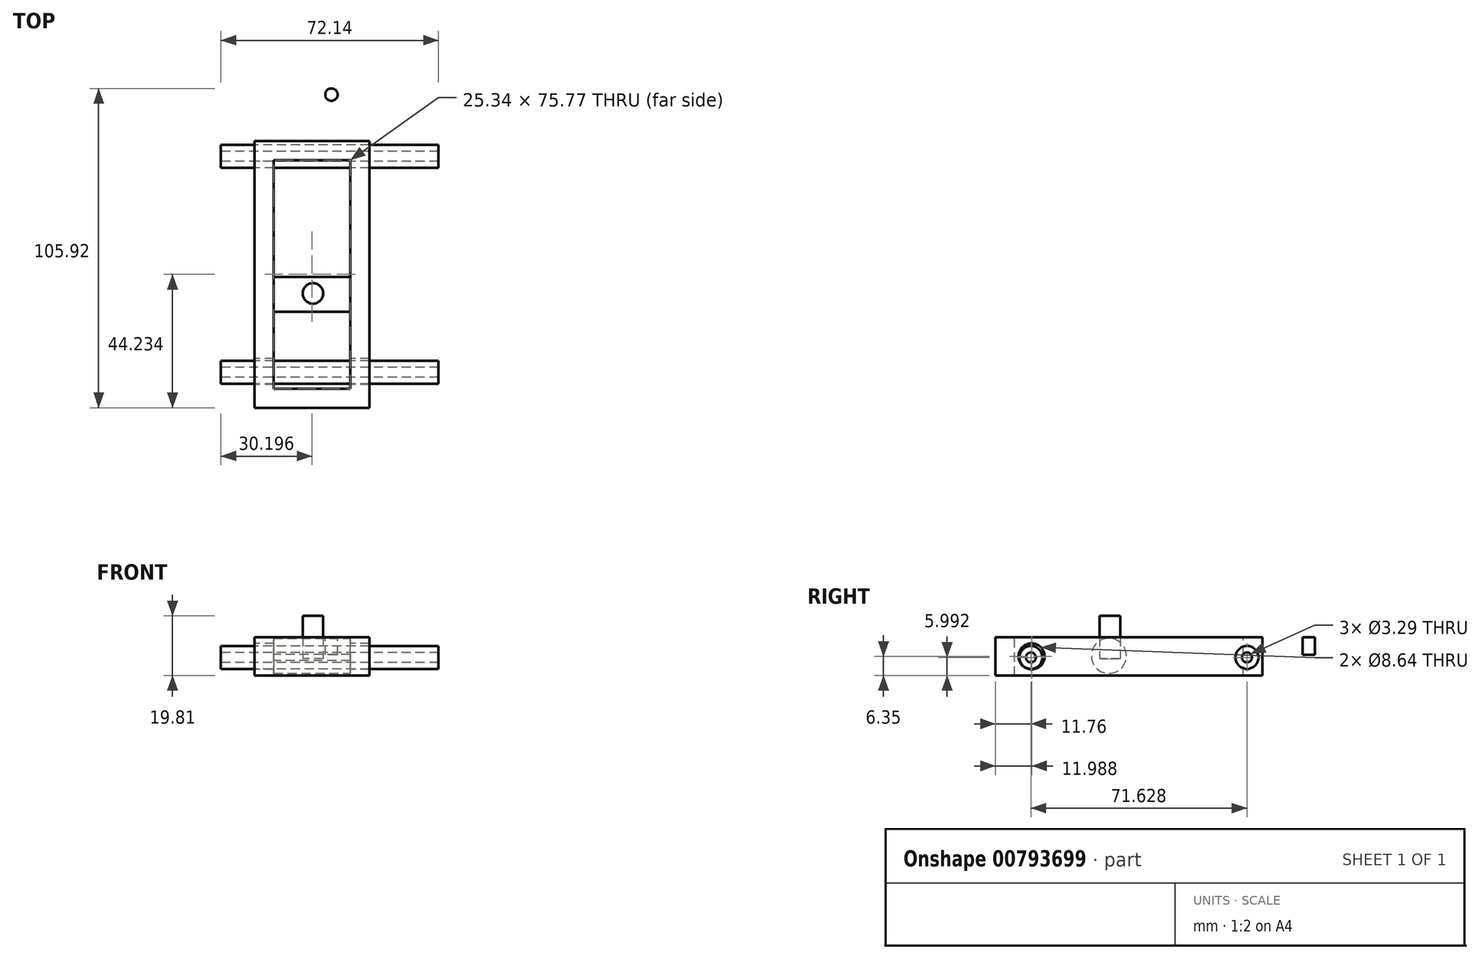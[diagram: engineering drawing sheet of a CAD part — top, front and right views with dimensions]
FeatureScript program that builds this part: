
annotation { "Feature Type Name" : "Feature", "Feature Type Description" : "" }
export const myFeature = defineFeature(function(context is Context, id is Id, definition is map)
    precondition{}
    {
        {
            var Q0;
            Q0=qCreatedBy(makeId("Top.planeOp"),FACE);
            var sketch = newSketch(context, id + "F0", { "sketchPlane" : qUnion([Q0])});
            skLineSegment(sketch, "E0.bottom", {"start": v(-27.68, 27.07) * mm, "end": v(10.35, 27.07) * mm});
            skLineSegment(sketch, "E0.top", {"start": v(-27.68, -61.4) * mm, "end": v(10.35, -61.4) * mm});
            skLineSegment(sketch, "E0.left", {"start": v(-27.68, 27.07) * mm, "end": v(-27.68, -61.4) * mm});
            skLineSegment(sketch, "E0.right", {"start": v(10.35, 27.07) * mm, "end": v(10.35, -61.4) * mm});
            skSolve(sketch);
        }
        {
            var Q0;
            Q0 = qSketchRegion(id + "F0", true);
            extrude(context, id + "F1", {"entities" : qUnion([Q0]), "depth" : 12.7 * mm, "offsetDistance" : 25.4 * mm});
        }
        {
            var Q0;
            Q0=makeQuery(id+"F1.opExtrude","CAP_FACE",FACE,{"disambiguationData":[OSD([sQuery(id+"F0.wireOp",EDGE,"E0.bottom"),sQuery(id+"F0.wireOp",EDGE,"E0.top"),sQuery(id+"F0.wireOp",EDGE,"E0.left"),sQuery(id+"F0.wireOp",EDGE,"E0.right")])],"isStart":false});
            var sketch = newSketch(context, id + "F2", { "sketchPlane" : qUnion([Q0])});
            skLineSegment(sketch, "E1.0", {"start": v(-21.33, 20.72) * mm, "end": v(4, 20.72) * mm});
            skLineSegment(sketch, "E1.1", {"start": v(-21.33, 20.72) * mm, "end": v(-21.33, -55.05) * mm});
            skLineSegment(sketch, "E1.2", {"start": v(-21.33, -55.05) * mm, "end": v(4, -55.05) * mm});
            skLineSegment(sketch, "E1.3", {"start": v(4, 20.72) * mm, "end": v(4, -55.05) * mm});
            skSolve(sketch);
        }
        {
            var Q0;
            Q0=makeQuery(id+"F2.imprint","IMPRINT",FACE,{"disambiguationData":[TD([[makeQuery(id+"F2.imprint","IMPRINT",EDGE,{"derivedFrom":sQuery(id+"F2.wireOp",EDGE,"E1.0")}),-1.0]])]});
            extrude(context, id + "F3", {"entities" : qUnion([Q0]), "operationType" : NewBodyOperationType.REMOVE, "oppositeDirection" : true, "depth" : 25.4 * mm, "offsetDistance" : 25.4 * mm});
        }
        {
            var Q0;
            Q0=makeQuery(id+"F1.opExtrude","SWEPT_FACE",FACE,{"disambiguationData":[OSD([sQuery(id+"F0.wireOp",EDGE,"E0.left")])]});
            var sketch = newSketch(context, id + "F4", { "sketchPlane" : qUnion([Q0])});
            skCircle(sketch, "E2", {"center": v(49.41, 6.35) * mm, "radius": 4.32 * mm});
            skSolve(sketch);
        }
        {
            var Q0;
            Q0 = qSketchRegion(id + "F4", true);
            var Q1;
            Q1=makeQuery(id+"F4.imprint","IMPRINT",FACE,{"disambiguationData":[TD([[makeQuery(id+"F4.imprint","IMPRINT",EDGE,{"derivedFrom":sQuery(id+"F4.wireOp",EDGE,"E2")}),1.0]])]});
            extrude(context, id + "F5", {"entities" : qUnion([Q0, Q1]), "operationType" : NewBodyOperationType.REMOVE, "oppositeDirection" : true, "depth" : 64.52 * mm, "offsetDistance" : 25.4 * mm});
        }
        {
            var Q0;
            Q0=makeQuery(id+"F1.opExtrude","SWEPT_FACE",FACE,{"disambiguationData":[OSD([sQuery(id+"F0.wireOp",EDGE,"E0.left")])]});
            var sketch = newSketch(context, id + "F6", { "sketchPlane" : qUnion([Q0])});
            skCircle(sketch, "E3", {"center": v(-21.99, 6) * mm, "radius": 1.65 * mm});
            skSolve(sketch);
        }
        {
            var Q0;
            Q0 = qSketchRegion(id + "F6", true);
            extrude(context, id + "F7", {"entities" : qUnion([Q0]), "operationType" : NewBodyOperationType.REMOVE, "oppositeDirection" : true, "depth" : 67.3 * mm, "offsetDistance" : 25.4 * mm});
        }
        {
            var Q0;
            Q0=makeQuery(id+"F1.opExtrude","SWEPT_FACE",FACE,{"disambiguationData":[OSD([sQuery(id+"F0.wireOp",EDGE,"E0.left")])]});
            var sketch = newSketch(context, id + "F8", { "sketchPlane" : qUnion([Q0])});
            skCircle(sketch, "E4.0", {"center": v(-21.99, 6) * mm, "radius": 1.65 * mm});
            skCircle(sketch, "E5", {"center": v(-21.99, 6) * mm, "radius": 3.81 * mm});
            skSolve(sketch);
        }
        {
            var Q0;
            Q0=makeQuery(id+"F8.imprint","IMPRINT",FACE,{"disambiguationData":[TD([[makeQuery(id+"F8.imprint","IMPRINT",EDGE,{"derivedFrom":sQuery(id+"F8.wireOp",EDGE,"E5")}),1.0]])]});
            extrude(context, id + "F9", {"entities" : qUnion([Q0]), "oppositeDirection" : true, "depth" : 72.14 * mm, "offsetDistance" : 25.4 * mm});
        }
        {
            var Q0;
            Q0=makeQuery(id+"F9.opExtrude","SWEPT_BODY",BODY,{"disambiguationData":[OSD([sQuery(id+"F8.wireOp",EDGE,"E4.0"),sQuery(id+"F8.wireOp",EDGE,"E5")])]});
            transform(context, id + "F10", {"entities" : qUnion([Q0]), "transformType" : TransformType.TRANSLATION_3D, "dx" : -11.18 * mm, "dy" : 0 * mm, "dz" : 0 * mm, "makeCopy" : false});
        }
        {
            var Q0;
            Q0=makeQuery(id+"F9.opExtrude","SWEPT_BODY",BODY,{"disambiguationData":[OSD([sQuery(id+"F8.wireOp",EDGE,"E5")])]});
            transform(context, id + "F11", {"entities" : qUnion([Q0]), "transformType" : TransformType.TRANSLATION_3D, "dx" : 0 * mm, "dy" : -71.63 * mm, "dz" : 0 * mm, "makeCopy" : true});
        }
        {
            var Q0;
            Q0=makeQuery(id+"F3.boolean.opBoolean","COPY",FACE,{"derivedFrom":makeQuery(id+"F3.opExtrude","SWEPT_FACE",FACE,{"disambiguationData":[OSD([sQuery(id+"F2.wireOp",EDGE,"E1.3")])]})});
            var sketch = newSketch(context, id + "F12", { "sketchPlane" : qUnion([Q0])});
            skCircle(sketch, "E6", {"center": v(23.79, 6.52) * mm, "radius": 5.81 * mm});
            skSolve(sketch);
        }
        {
            var Q0;
            Q0 = qSketchRegion(id + "F12", true);
            extrude(context, id + "F13", {"entities" : qUnion([Q0]), "operationType" : NewBodyOperationType.ADD, "depth" : 29.46 * mm, "offsetDistance" : 25.4 * mm});
        }
        {
            var Q0;
            Q0=makeQuery(id+"F1.opExtrude","CAP_FACE",FACE,{"disambiguationData":[OSD([sQuery(id+"F0.wireOp",EDGE,"E0.bottom"),sQuery(id+"F0.wireOp",EDGE,"E0.top"),sQuery(id+"F0.wireOp",EDGE,"E0.left"),sQuery(id+"F0.wireOp",EDGE,"E0.right")])],"isStart":false});
            var sketch = newSketch(context, id + "F14", { "sketchPlane" : qUnion([Q0])});
            skCircle(sketch, "E7", {"center": v(-8.35, -23.47) * mm, "radius": 3.4 * mm});
            skSolve(sketch);
        }
        {
            var Q0;
            Q0 = qSketchRegion(id + "F14", true);
            extrude(context, id + "F15", {"entities" : qUnion([Q0]), "depth" : 14.22 * mm, "offsetDistance" : 25.4 * mm, "symmetric" : true});
        }
        {
            var Q0;
            Q0=makeQuery(id+"F1.opExtrude","CAP_FACE",FACE,{"disambiguationData":[OSD([sQuery(id+"F0.wireOp",EDGE,"E0.bottom"),sQuery(id+"F0.wireOp",EDGE,"E0.top"),sQuery(id+"F0.wireOp",EDGE,"E0.left"),sQuery(id+"F0.wireOp",EDGE,"E0.right")])],"isStart":false});
            var sketch = newSketch(context, id + "F16", { "sketchPlane" : qUnion([Q0])});
            skCircle(sketch, "E8", {"center": v(-2.22, 42.46) * mm, "radius": 2.06 * mm});
            skSolve(sketch);
        }
        {
            var Q0;
            Q0 = qSketchRegion(id + "F16", true);
            extrude(context, id + "F17", {"entities" : qUnion([Q0]), "operationType" : NewBodyOperationType.ADD, "oppositeDirection" : true, "depth" : 5.84 * mm, "offsetDistance" : 25.4 * mm});
        }
    });
